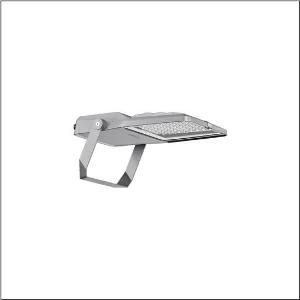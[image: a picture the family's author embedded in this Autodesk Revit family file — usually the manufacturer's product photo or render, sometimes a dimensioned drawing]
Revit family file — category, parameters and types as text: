
# Revit family: floodlight_fl_21_iq_mini___pl33t_5xa7772d3f1a_bc4e
name_source: partatom
category: Lighting Fixtures
units: mm (PartAtom-declared; Revit-internal decimal feet)

## family parameters
Cut with Voids When Loaded = No
Host = Face
Light Source = No
Part Type = Normal
Room Calculation Point = No
Round Connector Dimension = Use Diameter
Shared = No

## types (1)
- --- (1 x LED, 15160 lm, 143 W, 3000K)
    Apparent Load = 143 VA
    CIE Flux Codes = 26 75 99 100 100
    Color Rendering = 80
    Color Temperature = 3000K
    Default Elevation = 1800 mm
    Description = Floodlight FL 21 iQ mini, floodlight, primary light control with lens, of PMMA, primary optical cover: protective disc, of toughened safety glass, transparent, light distribution: PL33T, light emission: direct distribution, installation type: surface-mounted, LED, High Power LED, rated luminous flux: 15.160lm, luminous efficacy: 106lm/W, light colour: 830, colour temperature: 3000K, control: Street-Remote, Auto-Match, Temp-Guard, Night-Set, Smart-Wire, Desk-Remote (wireless, voltage-free reading and setting of iQ features in the workshop via application-optimized NFC function/RFID function), optimised constant luminous flux control (CLO 2.0), with terminal, 6-pole, mains connection: 220..240V, AC, 50/60Hz, start of lifetime: 143W, end of service life: 152W, reduction: 61W, luminaire housing, of diecast aluminium, powder-coated, Siteco® metallic grey (DB 702S), corrosivity category C5 mid according to DIN EN ISO 12944, sealing non-destructively replaceable, mounting bracket, of steel, galvanised, powder-coated, Siteco® metallic grey (DB 702S), protection rating (complete): IP66, insulation class (complete): insulation class II (safety insulation), certification: CE, ENEC, VDE, protection symbol: D, impact resistance: IK08, permissible operating ambient temperature: -40..+40°C, permissible operating ambient temperature for outdoor applications: -40..+50°C, standard: DIN EN 12944, LABS conformity tested according to VDMA 24364:2018-05, packaging unit: 1 piece

Light Distribution: PL33T
    Height = 70 mm
    Lamp = 1 x LED
    Lamp Light Flux = 15160 lm
    Lamp Power = 143 W
    Lamp count = 1
    Length = 485 mm
    Luminous efficacy = 106 lm/W
    Manufacturer = Siteco
    ModVariant = No
    Model = 5XA7772D3F1A
    Number of Poles = 1
    OnlyDefault = Yes
    Power Factor = 1
    Product Name = Floodlight FL 21 iQ mini | PL33T
    Product group = floodlight | pylon annexe
    ProductGroupID = 6200
    Protection Class = Protection class II
    Protection Degree = IP 66
    RLX_Detail_Level = 1
    RLX_Emergency_Light_Flux = 0 lm
    RLX_Emergency_Type = 0
    RLX_Emergency_Type_DB = No
    RlxData = <blob elided: 96377 chars, md5=f9974e5d>
    Socket = socket
    Standby Power = 0 W
    System Light Flux = 15160 lm
    System Power = 143 W
    Type Comments = factory setting: luminous flux: 100 % | dim-lin: 254 | 730 mA
    Type Image = l_1006845.jpg
    URL = http://relux.com
    VarID = @adj_099051
    Voltage = 0 V
    Weight = 0.00 kg
    Width = 337 mm

## geometry (parser evidence)
native form markers: Blend x4, Sweep x14
no freeform markers — native parametric forms only
